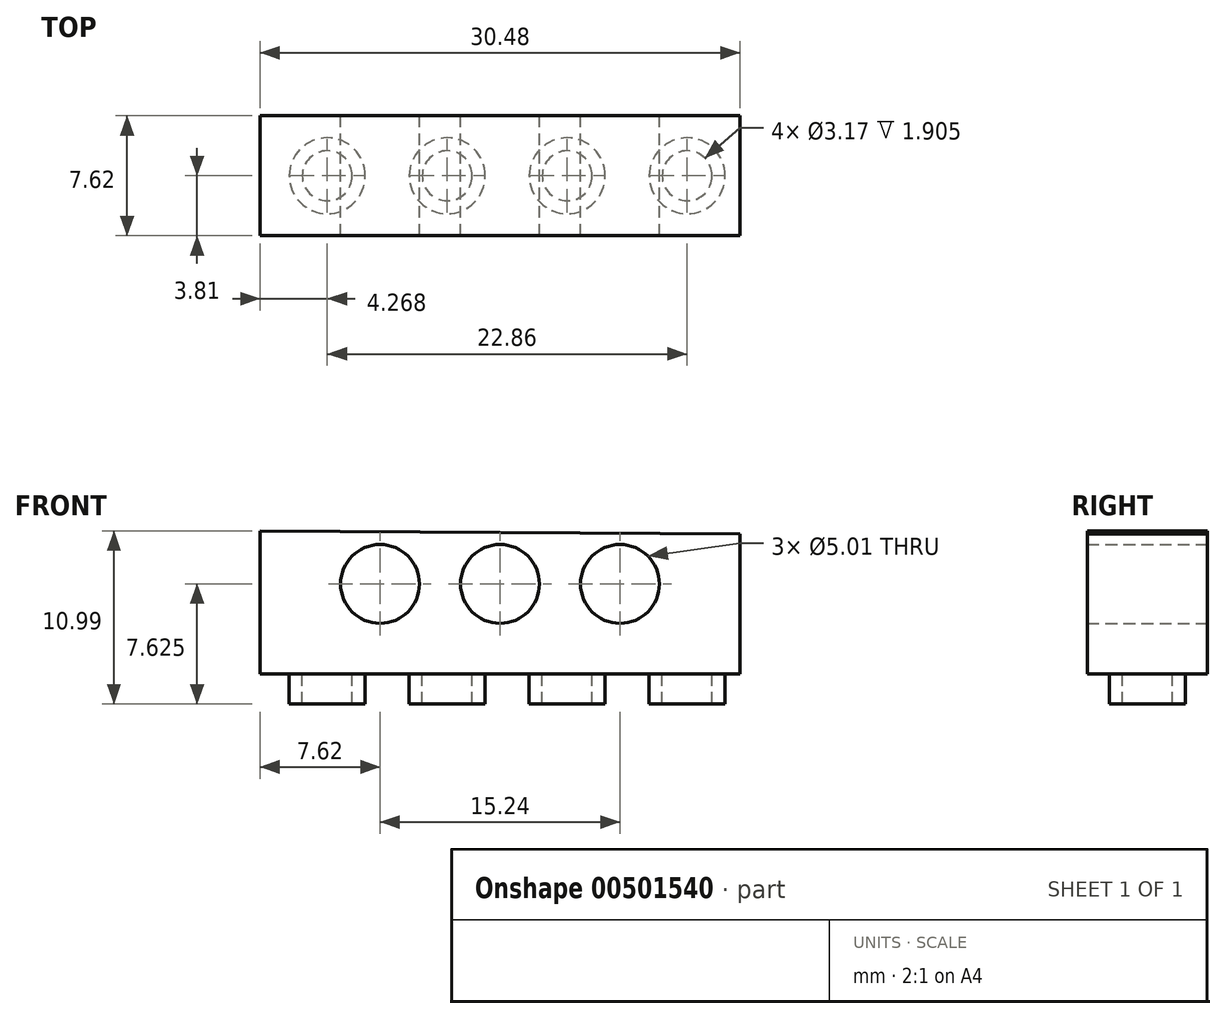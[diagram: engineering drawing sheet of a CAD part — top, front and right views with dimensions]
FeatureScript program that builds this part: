
annotation { "Feature Type Name" : "Feature", "Feature Type Description" : "" }
export const myFeature = defineFeature(function(context is Context, id is Id, definition is map)
    precondition{}
    {
        {
            var Q0;
            Q0=qCreatedBy(makeId("Front.planeOp"),FACE);
            var sketch = newSketch(context, id + "F0", { "sketchPlane" : qUnion([Q0])});
            skLineSegment(sketch, "E0", {"start": v(0, 9.08) * mm, "end": v(0, 0) * mm});
            skLineSegment(sketch, "E1", {"start": v(0, 0) * mm, "end": v(30.48, 0) * mm});
            skLineSegment(sketch, "E2", {"start": v(30.48, 0) * mm, "end": v(30.48, 8.9) * mm});
            skLineSegment(sketch, "E3", {"start": v(30.48, 8.9) * mm, "end": v(0, 9.08) * mm});
            skCircle(sketch, "E4", {"center": v(7.62, 5.72) * mm, "radius": 2.92 * mm});
            skCircle(sketch, "E5", {"center": v(7.62, 5.72) * mm, "radius": 2.5 * mm});
            skCircle(sketch, "E6.1.0.0", {"center": v(15.24, 5.71) * mm, "radius": 2.92 * mm});
            skCircle(sketch, "E6.1.0.1", {"center": v(15.24, 5.71) * mm, "radius": 2.5 * mm});
            skCircle(sketch, "E6.2.0.0", {"center": v(22.86, 5.71) * mm, "radius": 2.92 * mm});
            skCircle(sketch, "E6.2.0.1", {"center": v(22.86, 5.71) * mm, "radius": 2.5 * mm});
            skLineSegment(sketch, "E6.direction1", {"start": v(7.62, 5.71) * mm, "end": v(15.24, 5.71) * mm, "construction": true});
            skSolve(sketch);
        }
        {
            var Q0;
            Q0=makeQuery(id+"F0.imprint","IMPRINT",FACE,{"disambiguationData":[TD([[makeQuery(id+"F0.imprint","IMPRINT",EDGE,{"derivedFrom":sQuery(id+"F0.wireOp",EDGE,"E0")}),1.0]])]});
            var Q1;
            Q1=makeQuery(id+"F0.imprint","IMPRINT",FACE,{"disambiguationData":[TD([[makeQuery(id+"F0.imprint","IMPRINT",EDGE,{"derivedFrom":sQuery(id+"F0.wireOp",EDGE,"E6.1.0.0")}),1.0]])]});
            var Q2;
            Q2=makeQuery(id+"F0.imprint","IMPRINT",FACE,{"disambiguationData":[TD([[makeQuery(id+"F0.imprint","IMPRINT",EDGE,{"derivedFrom":sQuery(id+"F0.wireOp",EDGE,"E6.2.0.0")}),1.0]])]});
            var Q3;
            Q3=makeQuery(id+"F0.imprint","IMPRINT",FACE,{"disambiguationData":[TD([[makeQuery(id+"F0.imprint","IMPRINT",EDGE,{"derivedFrom":sQuery(id+"F0.wireOp",EDGE,"E4")}),1.0]])]});
            extrude(context, id + "F1", {"entities" : qUnion([Q0, Q1, Q2, Q3]), "depth" : 7.62 * mm});
        }
        {
            var Q0;
            Q0=qCreatedBy(makeId("Top.planeOp"),FACE);
            var sketch = newSketch(context, id + "F2", { "sketchPlane" : qUnion([Q0])});
            skCircle(sketch, "E7", {"center": v(4.27, -3.81) * mm, "radius": 2.41 * mm});
            skCircle(sketch, "E8", {"center": v(4.27, -3.81) * mm, "radius": 1.59 * mm});
            skCircle(sketch, "E9.1.0.0", {"center": v(11.89, -3.81) * mm, "radius": 2.41 * mm});
            skCircle(sketch, "E9.1.0.1", {"center": v(11.89, -3.81) * mm, "radius": 1.59 * mm});
            skCircle(sketch, "E9.2.0.0", {"center": v(19.5, -3.81) * mm, "radius": 2.41 * mm});
            skCircle(sketch, "E9.2.0.1", {"center": v(19.5, -3.81) * mm, "radius": 1.59 * mm});
            skCircle(sketch, "E9.3.0.0", {"center": v(27.13, -3.81) * mm, "radius": 2.41 * mm});
            skCircle(sketch, "E9.3.0.1", {"center": v(27.13, -3.81) * mm, "radius": 1.59 * mm});
            skLineSegment(sketch, "E9.direction1", {"start": v(4.27, -3.81) * mm, "end": v(11.89, -3.81) * mm, "construction": true});
            skSolve(sketch);
        }
        {
            var Q0;
            Q0=makeQuery(id+"F2.imprint","IMPRINT",FACE,{"disambiguationData":[TD([[makeQuery(id+"F2.imprint","IMPRINT",EDGE,{"derivedFrom":sQuery(id+"F2.wireOp",EDGE,"E7")}),1.0]])]});
            var Q1;
            Q1=makeQuery(id+"F2.imprint","IMPRINT",FACE,{"disambiguationData":[TD([[makeQuery(id+"F2.imprint","IMPRINT",EDGE,{"derivedFrom":sQuery(id+"F2.wireOp",EDGE,"E9.1.0.0")}),1.0]])]});
            var Q2;
            Q2=makeQuery(id+"F2.imprint","IMPRINT",FACE,{"disambiguationData":[TD([[makeQuery(id+"F2.imprint","IMPRINT",EDGE,{"derivedFrom":sQuery(id+"F2.wireOp",EDGE,"E9.2.0.0")}),1.0]])]});
            var Q3;
            Q3=makeQuery(id+"F2.imprint","IMPRINT",FACE,{"disambiguationData":[TD([[makeQuery(id+"F2.imprint","IMPRINT",EDGE,{"derivedFrom":sQuery(id+"F2.wireOp",EDGE,"E9.3.0.0")}),1.0]])]});
            extrude(context, id + "F3", {"entities" : qUnion([Q0, Q1, Q2, Q3]), "operationType" : NewBodyOperationType.ADD, "oppositeDirection" : true, "depth" : 1.9 * mm});
        }
    });
